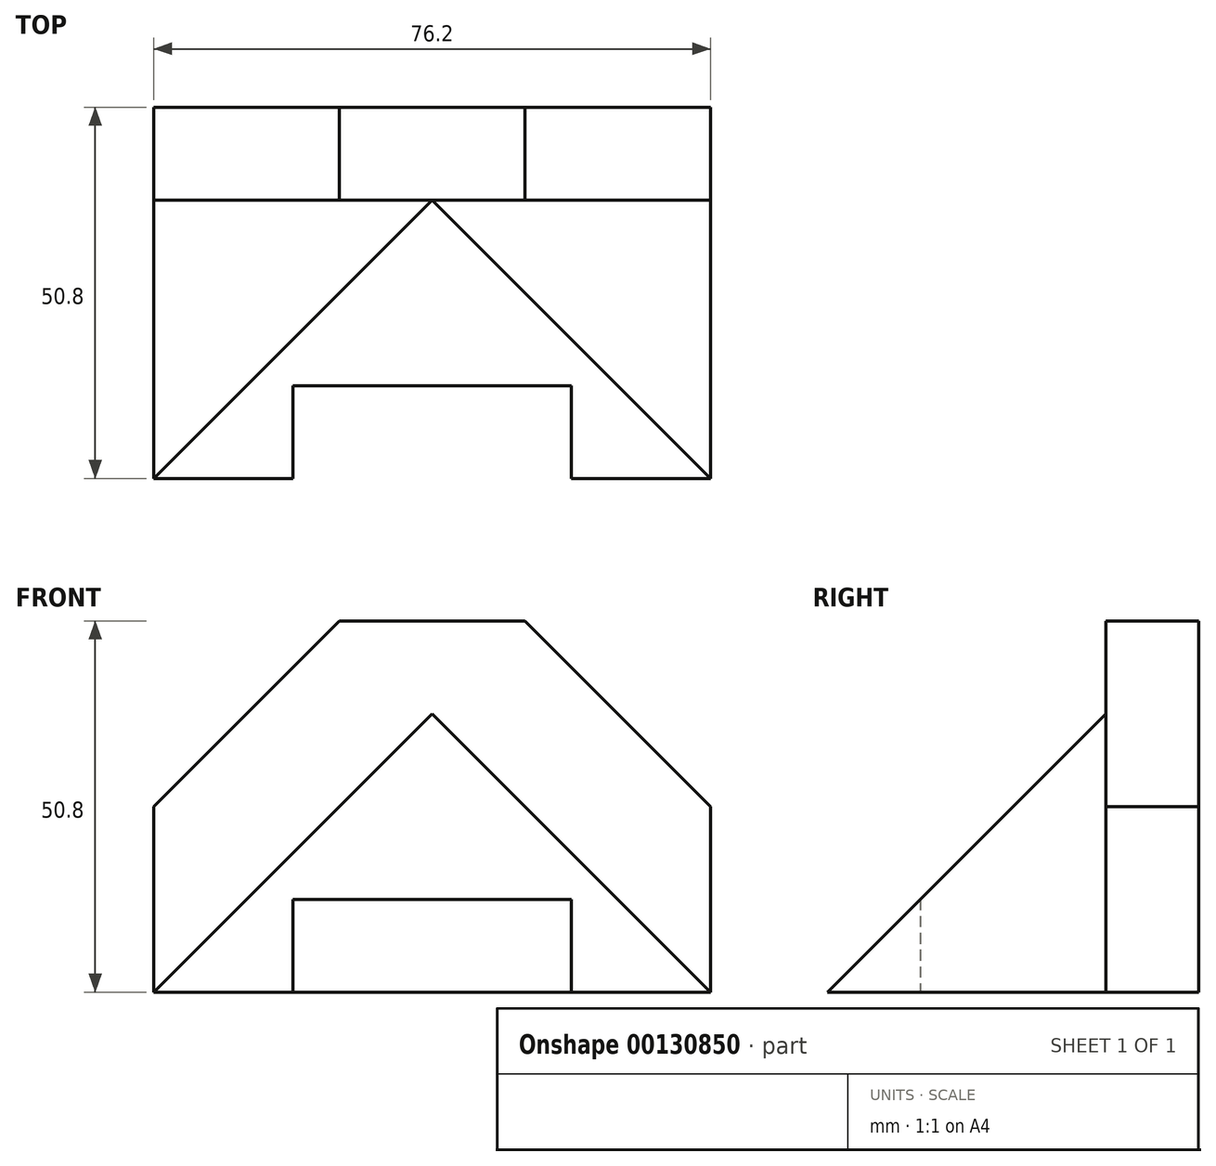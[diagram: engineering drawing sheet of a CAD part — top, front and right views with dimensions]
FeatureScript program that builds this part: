
annotation { "Feature Type Name" : "Feature", "Feature Type Description" : "" }
export const myFeature = defineFeature(function(context is Context, id is Id, definition is map)
    precondition{}
    {
        {
            var Q0;
            Q0=qCreatedBy(makeId("Front.planeOp"),FACE);
            var sketch = newSketch(context, id + "F0", { "sketchPlane" : qUnion([Q0])});
            skLineSegment(sketch, "E0", {"start": v(-38.1, 0) * mm, "end": v(0, 0) * mm});
            skLineSegment(sketch, "E1", {"start": v(0, 0) * mm, "end": v(38.1, 0) * mm});
            skLineSegment(sketch, "E2", {"start": v(38.1, 0) * mm, "end": v(0, 38.1) * mm});
            skLineSegment(sketch, "E3", {"start": v(0, 38.1) * mm, "end": v(-38.1, 0) * mm});
            skSolve(sketch);
        }
        {
            var Q0;
            Q0 = qSketchRegion(id + "F0", true);
            extrude(context, id + "F1", {"entities" : qUnion([Q0]), "depth" : 38.1 * mm});
        }
        {
            var Q0;
            Q0=qCreatedBy(makeId("Right.planeOp"),FACE);
            var sketch = newSketch(context, id + "F2", { "sketchPlane" : qUnion([Q0])});
            skLineSegment(sketch, "E4", {"start": v(0, 38.1) * mm, "end": v(-38.1, 0) * mm});
            skLineSegment(sketch, "E5", {"start": v(-38.1, 0) * mm, "end": v(-38.1, 38.1) * mm});
            skLineSegment(sketch, "E6", {"start": v(-38.1, 38.1) * mm, "end": v(0, 38.1) * mm});
            skSolve(sketch);
        }
        {
            var Q0;
            Q0 = qSketchRegion(id + "F2", true);
            extrude(context, id + "F3", {"entities" : qUnion([Q0]), "operationType" : NewBodyOperationType.REMOVE, "endBound" : BoundingType.SYMMETRIC, "depth" : 6 * 12.95 * mm});
        }
        {
            var Q0;
            Q0=qCreatedBy(makeId("Top.planeOp"),FACE);
            var sketch = newSketch(context, id + "F4", { "sketchPlane" : qUnion([Q0])});
            skLineSegment(sketch, "E7", {"start": v(0, -38.1) * mm, "end": v(19.05, -38.1) * mm});
            skLineSegment(sketch, "E8", {"start": v(19.05, -38.1) * mm, "end": v(19.05, -25.4) * mm});
            skLineSegment(sketch, "E9", {"start": v(19.05, -25.4) * mm, "end": v(-19.05, -25.4) * mm});
            skLineSegment(sketch, "E10", {"start": v(-19.05, -25.4) * mm, "end": v(-19.05, -38.1) * mm});
            skLineSegment(sketch, "E11", {"start": v(-19.05, -38.1) * mm, "end": v(0, -38.1) * mm});
            skSolve(sketch);
        }
        {
            var Q0;
            Q0 = qSketchRegion(id + "F4", true);
            extrude(context, id + "F5", {"entities" : qUnion([Q0]), "operationType" : NewBodyOperationType.REMOVE, "endBound" : BoundingType.THROUGH_ALL, "depth" : 25.4 * mm});
        }
        {
            var Q0;
            Q0=makeQuery(id+"F1.opExtrude","CAP_FACE",FACE,{"disambiguationData":[OSD([sQuery(id+"F0.wireOp",EDGE,"E0"),sQuery(id+"F0.wireOp",EDGE,"E1"),sQuery(id+"F0.wireOp",EDGE,"E2"),sQuery(id+"F0.wireOp",EDGE,"E3")])],"isStart":true});
            var sketch = newSketch(context, id + "F6", { "sketchPlane" : qUnion([Q0])});
            skLineSegment(sketch, "E12", {"start": v(0, 0) * mm, "end": v(38.1, 0) * mm});
            skLineSegment(sketch, "E13", {"start": v(38.1, 0) * mm, "end": v(38.1, 25.4) * mm});
            skLineSegment(sketch, "E14", {"start": v(38.1, 25.4) * mm, "end": v(12.7, 50.8) * mm});
            skLineSegment(sketch, "E15", {"start": v(12.7, 50.8) * mm, "end": v(-12.7, 50.8) * mm});
            skLineSegment(sketch, "E16", {"start": v(-12.7, 50.8) * mm, "end": v(-38.1, 25.4) * mm});
            skLineSegment(sketch, "E17", {"start": v(-38.1, 25.4) * mm, "end": v(-38.1, 0) * mm});
            skLineSegment(sketch, "E18", {"start": v(-38.1, 0) * mm, "end": v(0, 0) * mm});
            skSolve(sketch);
        }
        {
            var Q0;
            Q0 = qSketchRegion(id + "F6", true);
            extrude(context, id + "F7", {"entities" : qUnion([Q0]), "operationType" : NewBodyOperationType.ADD, "depth" : 12.7 * mm});
        }
    });
